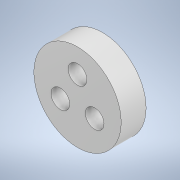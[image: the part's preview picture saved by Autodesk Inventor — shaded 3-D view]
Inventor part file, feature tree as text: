
AUTODESK INVENTOR PART (.ipt)
format: ipt  version: 2020.2 (Build 242310000, 310)  size: 128,000 bytes
history: native  units: mm
features: sketch x3, projected_geometry x2, other x1, extrude x1
ambient origin geometry x8: Origin, YZ Plane, XZ Plane, XY Plane, X Axis, Y Axis, Z Axis, Center Point
bodies: Body1 (feature_tree)
feature tree (7):
  other  "ソリッド1"
  extrude  "押し出し1"  Depth=3.0mm
  sketch  "スケッチ2"
  sketch  "スケッチ3"
  sketch  "スケッチ1"
  projected_geometry  "投影ループ1"
  projected_geometry  "投影ループ2"
